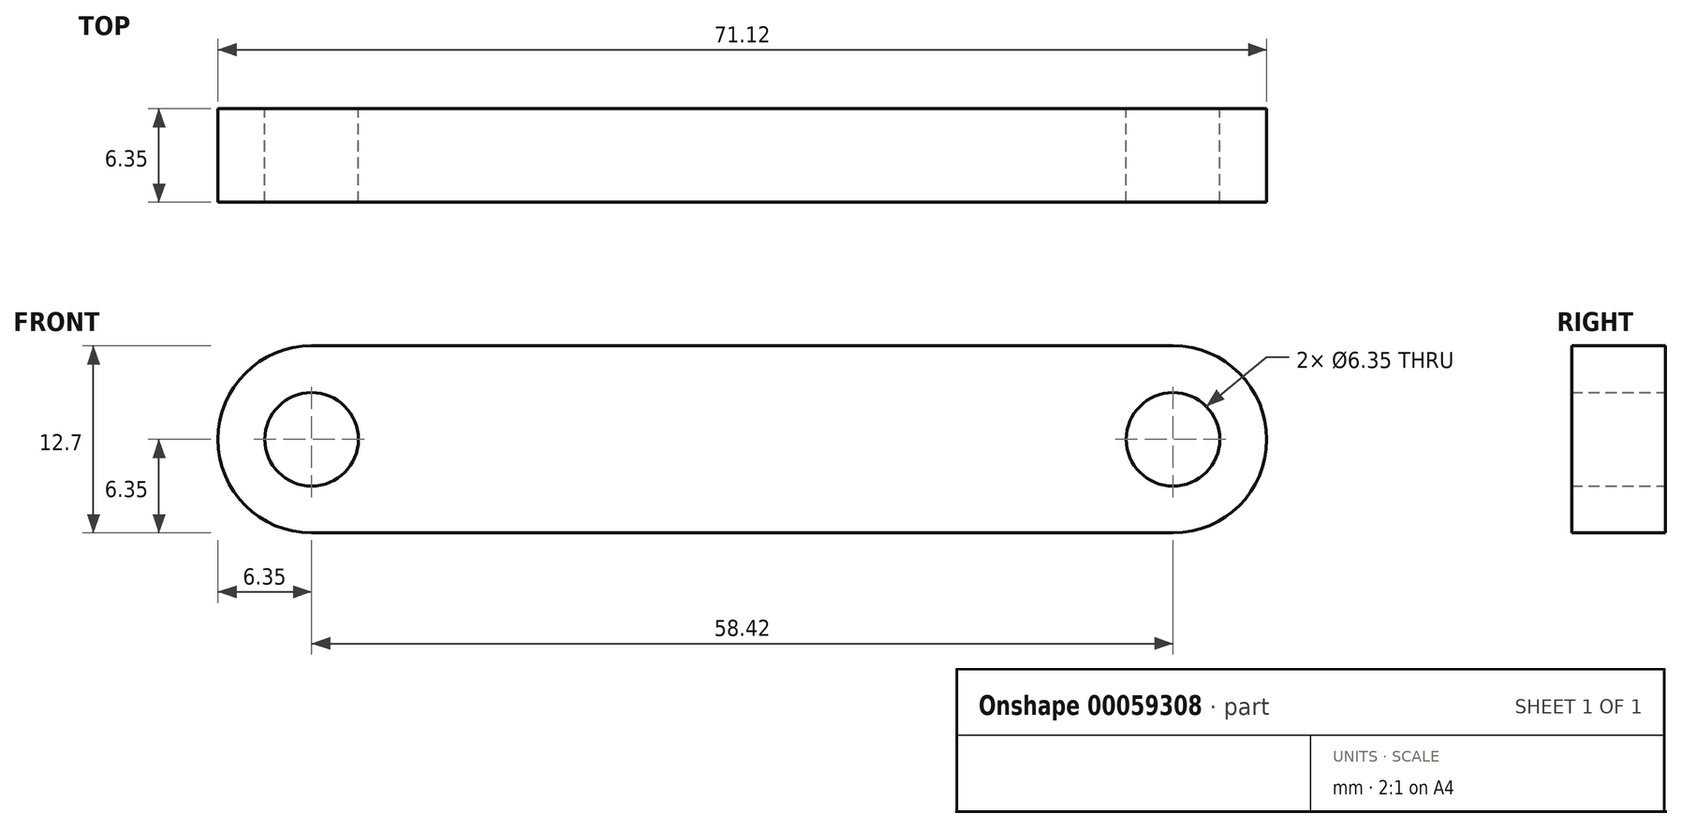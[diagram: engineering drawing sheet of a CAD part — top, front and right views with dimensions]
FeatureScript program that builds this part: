
annotation { "Feature Type Name" : "Feature", "Feature Type Description" : "" }
export const myFeature = defineFeature(function(context is Context, id is Id, definition is map)
    precondition{}
    {
        {
            var Q0;
            Q0=qCreatedBy(makeId("Front.planeOp"),FACE);
            var sketch = newSketch(context, id + "F0", { "sketchPlane" : qUnion([Q0])});
            skLineSegment(sketch, "E0", {"start": v(-29.2, 6.35) * mm, "end": v(29.21, 6.35) * mm});
            skLineSegment(sketch, "E1", {"start": v(-29.21, -6.35) * mm, "end": v(29.2, -6.35) * mm});
            skArc(sketch, "E2", {"start": v(-29.2, 6.35) * mm, "mid": v(-35.56, 0) * mm, "end": v(-29.21, -6.35) * mm});
            skArc(sketch, "E3", {"start": v(29.2, -6.35) * mm, "mid": v(35.56, 0) * mm, "end": v(29.21, 6.35) * mm});
            skCircle(sketch, "E4", {"center": v(-29.2, 0) * mm, "radius": 3.18 * mm});
            skCircle(sketch, "E5", {"center": v(29.21, 0) * mm, "radius": 3.18 * mm});
            skSolve(sketch);
        }
        {
            var Q0;
            Q0=makeQuery(id+"F0.imprint","IMPRINT",FACE,{"disambiguationData":[TD([[makeQuery(id+"F0.imprint","IMPRINT",EDGE,{"derivedFrom":sQuery(id+"F0.wireOp",EDGE,"E0")}),-1.0]])]});
            extrude(context, id + "F1", {"entities" : qUnion([Q0]), "depth" : 6.35 * mm});
        }
    });
